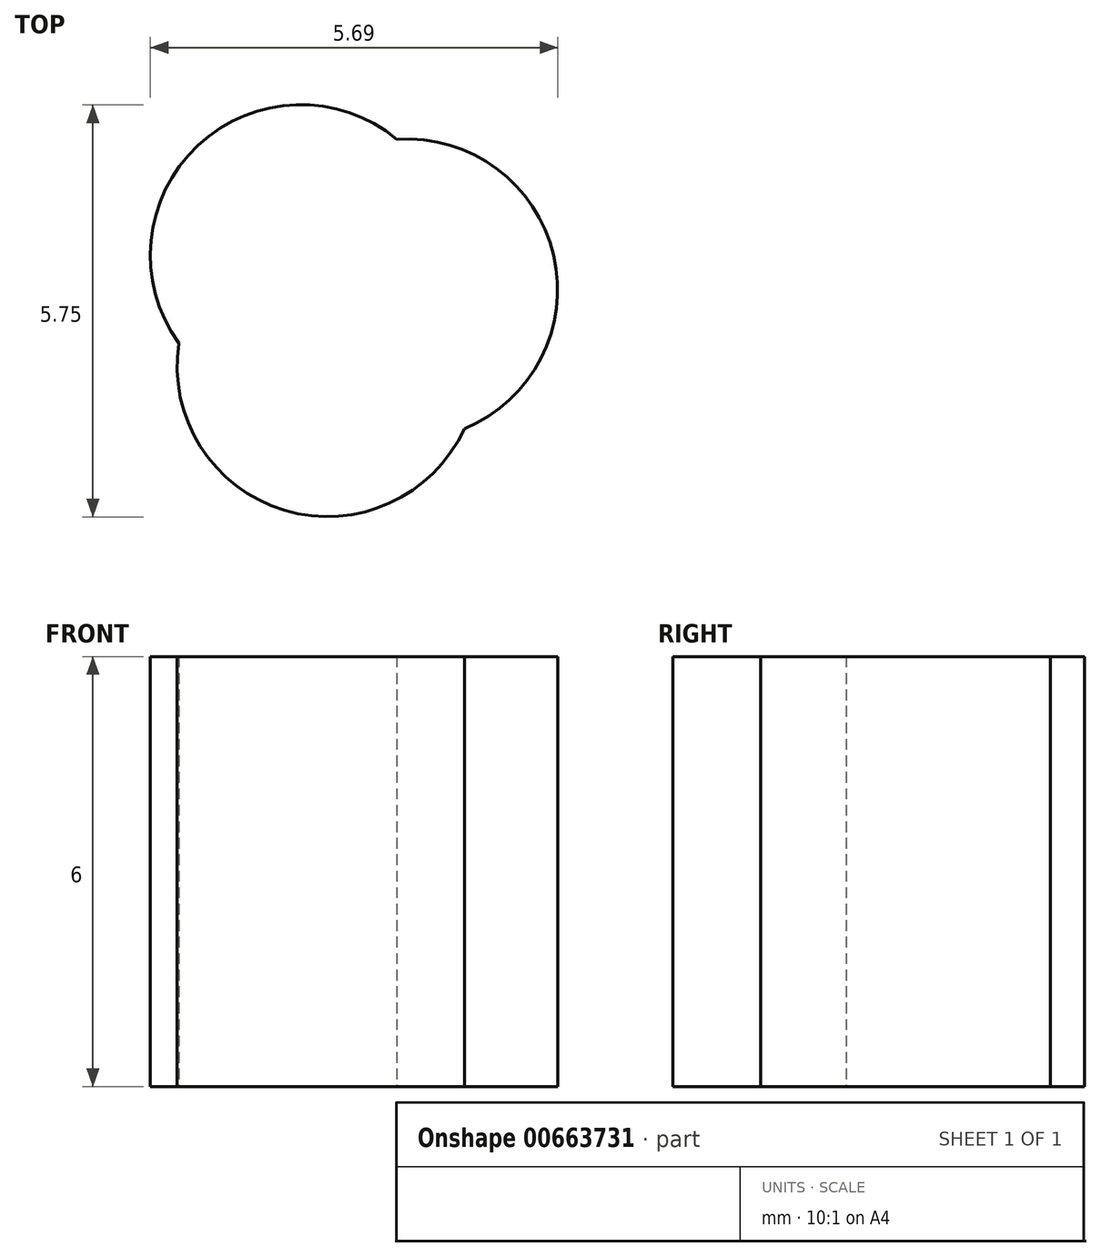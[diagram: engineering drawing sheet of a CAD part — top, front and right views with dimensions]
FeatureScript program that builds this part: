
annotation { "Feature Type Name" : "Feature", "Feature Type Description" : "" }
export const myFeature = defineFeature(function(context is Context, id is Id, definition is map)
    precondition{}
    {
        {
            var Q0;
            Q0=qCreatedBy(makeId("Top.planeOp"),FACE);
            var sketch = newSketch(context, id + "F0", { "sketchPlane" : qUnion([Q0])});
            skCircle(sketch, "E0", {"center": v(-0.59, 0.7) * mm, "radius": 2.1 * mm});
            skCircle(sketch, "E1.1.0", {"center": v(-0.22, -0.86) * mm, "radius": 2.1 * mm});
            skCircle(sketch, "E1.2.0", {"center": v(0.9, 0.21) * mm, "radius": 2.1 * mm});
            skPoint(sketch, "E1.center", {"position": v(0, 0) * mm});
            skSolve(sketch);
        }
        {
            var Q0;
            {var subQ0=sQuery(id+"F0.wireOp",EDGE,"E1.1.0");var subQ1=sQuery(id+"F0.wireOp",EDGE,"E0");var subQ2=makeQuery(id+"F0.imprint","INTERSECT",VERTEX,{"disambiguationData":[OD(0.0)],"derivedFrom":[subQ1,subQ0]});Q0=makeQuery(id+"F0.imprint","IMPRINT",FACE,{"disambiguationData":[TD([[makeQuery(id+"F0.imprint","IMPRINT",EDGE,{"disambiguationData":[TD([[subQ2,1.0]])],"derivedFrom":subQ1}),1.0]])]});}
            var Q1;
            {var subQ0=sQuery(id+"F0.wireOp",EDGE,"E1.2.0");var subQ1=sQuery(id+"F0.wireOp",EDGE,"E0");var subQ2=makeQuery(id+"F0.imprint","INTERSECT",VERTEX,{"disambiguationData":[OD(0.0)],"derivedFrom":[subQ1,subQ0]});Q1=makeQuery(id+"F0.imprint","IMPRINT",FACE,{"disambiguationData":[TD([[makeQuery(id+"F0.imprint","IMPRINT",EDGE,{"disambiguationData":[TD([[subQ2,1.0]])],"derivedFrom":subQ1}),1.0]])]});}
            var Q2;
            {var subQ0=sQuery(id+"F0.wireOp",EDGE,"E1.2.0");var subQ1=sQuery(id+"F0.wireOp",EDGE,"E0");var subQ2=makeQuery(id+"F0.imprint","INTERSECT",VERTEX,{"disambiguationData":[OD(0.0)],"derivedFrom":[subQ1,subQ0]});Q2=makeQuery(id+"F0.imprint","IMPRINT",FACE,{"disambiguationData":[TD([[makeQuery(id+"F0.imprint","IMPRINT",EDGE,{"disambiguationData":[TD([[subQ2,1.0]])],"derivedFrom":subQ1}),-1.0]])]});}
            var Q3;
            {var subQ0=sQuery(id+"F0.wireOp",EDGE,"E1.2.0");var subQ1=sQuery(id+"F0.wireOp",EDGE,"E0");var subQ2=makeQuery(id+"F0.imprint","INTERSECT",VERTEX,{"disambiguationData":[OD(1.0)],"derivedFrom":[subQ1,subQ0]});Q3=makeQuery(id+"F0.imprint","IMPRINT",FACE,{"disambiguationData":[TD([[makeQuery(id+"F0.imprint","IMPRINT",EDGE,{"disambiguationData":[TD([[subQ2,-1.0]])],"derivedFrom":subQ1}),1.0]])]});}
            var Q4;
            {var subQ0=sQuery(id+"F0.wireOp",EDGE,"E1.1.0");var subQ1=sQuery(id+"F0.wireOp",EDGE,"E0");var subQ2=makeQuery(id+"F0.imprint","INTERSECT",VERTEX,{"disambiguationData":[OD(0.0)],"derivedFrom":[subQ1,subQ0]});Q4=makeQuery(id+"F0.imprint","IMPRINT",FACE,{"disambiguationData":[TD([[makeQuery(id+"F0.imprint","IMPRINT",EDGE,{"disambiguationData":[TD([[subQ2,-1.0]])],"derivedFrom":subQ1}),1.0]])]});}
            var Q5;
            {var subQ0=sQuery(id+"F0.wireOp",EDGE,"E1.1.0");var subQ1=sQuery(id+"F0.wireOp",EDGE,"E0");var subQ2=makeQuery(id+"F0.imprint","INTERSECT",VERTEX,{"disambiguationData":[OD(0.0)],"derivedFrom":[subQ1,subQ0]});Q5=makeQuery(id+"F0.imprint","IMPRINT",FACE,{"disambiguationData":[TD([[makeQuery(id+"F0.imprint","IMPRINT",EDGE,{"disambiguationData":[TD([[subQ2,-1.0]])],"derivedFrom":subQ1}),-1.0]])]});}
            var Q6;
            {var subQ0=sQuery(id+"F0.wireOp",EDGE,"E1.2.0");var subQ1=sQuery(id+"F0.wireOp",EDGE,"E0");var subQ2=makeQuery(id+"F0.imprint","INTERSECT",VERTEX,{"disambiguationData":[OD(1.0)],"derivedFrom":[subQ1,subQ0]});Q6=makeQuery(id+"F0.imprint","IMPRINT",FACE,{"disambiguationData":[TD([[makeQuery(id+"F0.imprint","IMPRINT",EDGE,{"disambiguationData":[TD([[subQ2,-1.0]])],"derivedFrom":subQ1}),-1.0]])]});}
            extrude(context, id + "F1", {"entities" : qUnion([Q0, Q1, Q2, Q3, Q4, Q5, Q6]), "depth" : 6 * mm, "offsetDistance" : 25 * mm});
        }
    });
